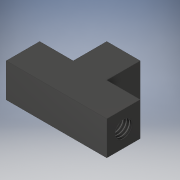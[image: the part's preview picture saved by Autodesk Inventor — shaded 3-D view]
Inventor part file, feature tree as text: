
AUTODESK INVENTOR PART (.ipt)
format: ipt  version: 2018.3 (Build 223285000, 285)  size: 147,968 bytes
history: native  units: mm
features: thread x3, imported_body x1
ambient origin geometry x8: Origin, YZ Plane, XZ Plane, XY Plane, X Axis, Y Axis, Z Axis, Center Point
bodies: Solid1 (feature_tree)
feature tree (4):
  imported_body  "Base1"
  thread  "Thread1"  [1 undecoded]
  thread  "Thread2"  [1 undecoded]
  thread  "Thread3"  [1 undecoded]
note: 3 required parameter values undecoded (feature->parameter linkage not recoverable at this tier; creation-order binding heuristic only, values carry confidence <= 0.55)
